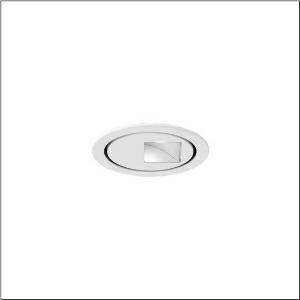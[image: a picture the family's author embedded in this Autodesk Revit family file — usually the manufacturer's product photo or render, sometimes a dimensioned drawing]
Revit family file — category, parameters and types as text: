
# Revit family: lunis_11_micro_round_51dj11b71wg21
name_source: partatom
category: Lighting Fixtures
units: mm (PartAtom-declared; Revit-internal decimal feet)

## family parameters
Cut with Voids When Loaded = No
Host = Face
Light Source = No
Part Type = Normal
Room Calculation Point = No
Round Connector Dimension = Use Diameter
Shared = No

## types (1)
- Lunis 11 micro round (1 x LED 4000K / CRI = 80 (unbekannt), 1400 lm, 4000K)
    Apparent Load = 20 VA
    CIE Flux Codes = 42 75 96 100 100
    Color Rendering = 80
    Color Temperature = 4000K
    Default Elevation = 1800 mm
    Description = Lunis 11 micro round, downlight, light control with wallwasher, of highly reflective aluminium, highly specular, light emission: direct distribution, LED rated luminous flux: 1.400lm, light colour: 840, control gear: ECG, with terminal, 3-pole, mains connection: 220..230V, AC/DC, 0/50..60Hz, LED module, luminaire module, of aluminium, highly specular, white, diameter: 114mm, clamping range: 1..40mm, recessing ring, of plastic, traffic white (RAL 9016), protection rating (complete): IP20, insulation class (complete): insulation class II (safety insulation), certification: CE, permissible ambient temperature for indoor applications: 0..+35°C, packaging unit: 1 piece
    Height = 0 mm  [stored 0 ft]
    Lamp = 1 x LED 4000K / CRI >= 80 (unbekannt)
    Lamp Light Flux = 1400 lm
    Lamp count = 1
    Length = 114 mm
    Luminous efficacy = 71 lm/W
    Manufacturer = Siteco
    ModVariant = No
    Model = 51DJ11B71WG21
    Mounting Place = Ceiling
    Mounting Type = Recessed
    Number of Poles = 1
    OnlyDefault = Yes
    Power Factor = 1
    Product Name = Lunis 11 micro round
    Product group = downlight | ceiling recessed
    ProductGroupID = 402
    Protection Class = Protection class II
    Protection Degree = IP 20
    RLX_Detail_Level = 1
    RlxData = <blob elided: 40677 chars, md5=e33ec24d>
    Socket = socket
    Standby Power = 0 W
    System Light Flux = 1400 lm
    System Power = 20 W
    Type Comments = Product without accessories
    Type Image = l_1004773.jpg
    URL = http://relux.com
    VarID = ---
    Voltage = 0 V
    Weight = 0.00 kg
    Width = 114 mm

note: [stored X ft] marks values corroborated as IEEE doubles in the binary element streams (Revit-internal decimal feet)

## geometry (parser evidence)
native form markers: Blend x4, Sweep x12
no freeform markers — native parametric forms only
